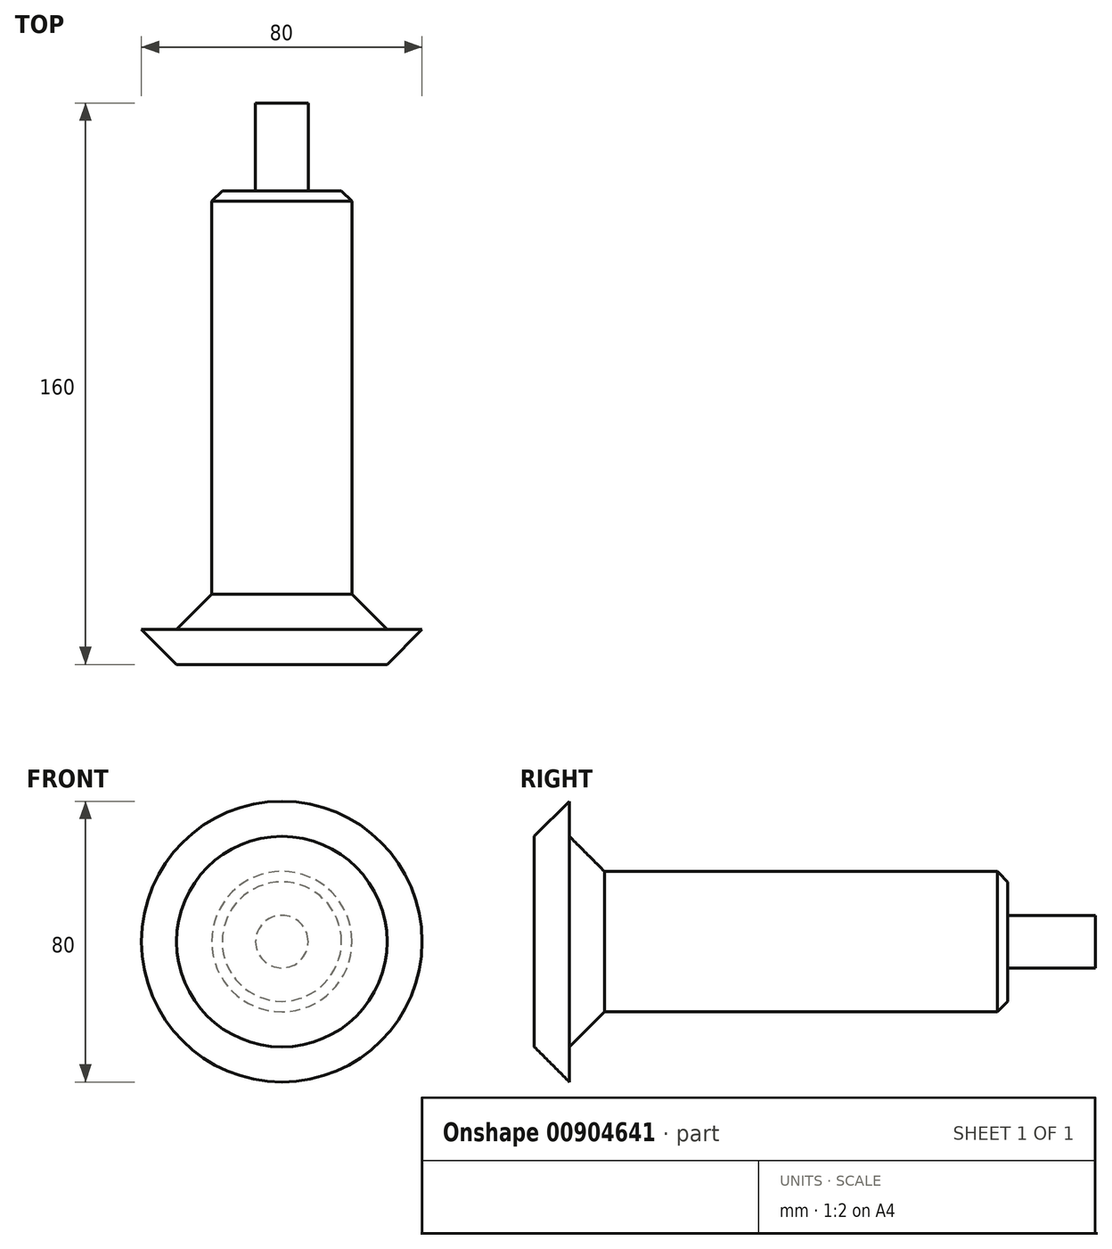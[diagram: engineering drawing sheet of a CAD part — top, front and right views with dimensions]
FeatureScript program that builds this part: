
annotation { "Feature Type Name" : "Feature", "Feature Type Description" : "" }
export const myFeature = defineFeature(function(context is Context, id is Id, definition is map)
    precondition{}
    {
        {
            var Q0;
            Q0=qCreatedBy(makeId("Front.planeOp"),FACE);
            var sketch = newSketch(context, id + "F0", { "sketchPlane" : qUnion([Q0])});
            skCircle(sketch, "E0", {"center": v(0, 0) * mm, "radius": 40 * mm});
            skSolve(sketch);
        }
        {
            var Q0;
            Q0=makeQuery(id+"F0.imprint","IMPRINT",FACE,{"disambiguationData":[TD([[makeQuery(id+"F0.imprint","IMPRINT",EDGE,{"derivedFrom":sQuery(id+"F0.wireOp",EDGE,"E0")}),1.0]])]});
            extrude(context, id + "F1", {"entities" : qUnion([Q0]), "depth" : 10 * mm, "offsetDistance" : 25.4 * mm});
        }
        {
            var Q0;
            Q0=makeQuery(id+"F1.opExtrude","CAP_FACE",FACE,{"disambiguationData":[OSD([sQuery(id+"F0.wireOp",EDGE,"E0")])],"isStart":true});
            var sketch = newSketch(context, id + "F2", { "sketchPlane" : qUnion([Q0])});
            skCircle(sketch, "E1", {"center": v(0, 0) * mm, "radius": 30 * mm});
            skSolve(sketch);
        }
        {
            var Q0;
            Q0=makeQuery(id+"F1.opExtrude","CAP_FACE",FACE,{"disambiguationData":[OSD([sQuery(id+"F0.wireOp",EDGE,"E0")])],"isStart":false});
            chamfer(context, id + "F3", {"entities" : qUnion([Q0]), "width" : 10 * mm, "tangentPropagation" : true});
        }
        {
            var Q0;
            Q0=makeQuery(id+"F2.imprint","IMPRINT",FACE,{"disambiguationData":[TD([[makeQuery(id+"F2.imprint","IMPRINT",EDGE,{"derivedFrom":sQuery(id+"F2.wireOp",EDGE,"E1")}),1.0]])]});
            extrude(context, id + "F4", {"entities" : qUnion([Q0]), "operationType" : NewBodyOperationType.ADD, "depth" : 10 * mm, "offsetDistance" : 25.4 * mm});
        }
        {
            var Q0;
            Q0=makeQuery(id+"F4.opExtrude","CAP_FACE",FACE,{"disambiguationData":[OSD([sQuery(id+"F2.wireOp",EDGE,"E1")])],"isStart":false});
            chamfer(context, id + "F5", {"entities" : qUnion([Q0]), "width" : 10 * mm, "tangentPropagation" : true});
        }
        {
            var Q0;
            Q0=makeQuery(id+"F4.opExtrude","CAP_FACE",FACE,{"disambiguationData":[OSD([sQuery(id+"F2.wireOp",EDGE,"E1")])],"isStart":false});
            var sketch = newSketch(context, id + "F6", { "sketchPlane" : qUnion([Q0])});
            skCircle(sketch, "E2", {"center": v(0, 0) * mm, "radius": 20 * mm});
            skSolve(sketch);
        }
        {
            var Q0;
            Q0=makeQuery(id+"F6.imprint","IMPRINT",FACE,{"disambiguationData":[TD([[makeQuery(id+"F6.imprint","IMPRINT",EDGE,{"derivedFrom":sQuery(id+"F6.wireOp",EDGE,"E2")}),1.0]])]});
            extrude(context, id + "F7", {"entities" : qUnion([Q0]), "operationType" : NewBodyOperationType.ADD, "depth" : 115 * mm, "offsetDistance" : 25.4 * mm});
        }
        {
            var Q0;
            Q0=makeQuery(id+"F7.opExtrude","CAP_EDGE",EDGE,{"disambiguationData":[OSD([sQuery(id+"F6.wireOp",EDGE,"E2")])],"isStart":false});
            chamfer(context, id + "F8", {"entities" : qUnion([Q0]), "width" : 3 * mm, "tangentPropagation" : true});
        }
        {
            var Q0;
            Q0=makeQuery(id+"F7.opExtrude","CAP_FACE",FACE,{"disambiguationData":[OSD([sQuery(id+"F6.wireOp",EDGE,"E2")])],"isStart":false});
            var sketch = newSketch(context, id + "F9", { "sketchPlane" : qUnion([Q0])});
            skCircle(sketch, "E3", {"center": v(0, 0) * mm, "radius": 7.5 * mm});
            skSolve(sketch);
        }
        {
            var Q0;
            Q0=makeQuery(id+"F9.imprint","IMPRINT",FACE,{"disambiguationData":[TD([[makeQuery(id+"F9.imprint","IMPRINT",EDGE,{"derivedFrom":sQuery(id+"F9.wireOp",EDGE,"E3")}),1.0]])]});
            var Q1;
            Q1=sQuery(id+"F9.wireOp",EDGE,"E3");
            extrude(context, id + "F10", {"entities" : qUnion([Q0]), "operationType" : NewBodyOperationType.ADD, "surfaceEntities" : qUnion([Q1]), "depth" : 25 * mm, "offsetDistance" : 25.4 * mm});
        }
    });
